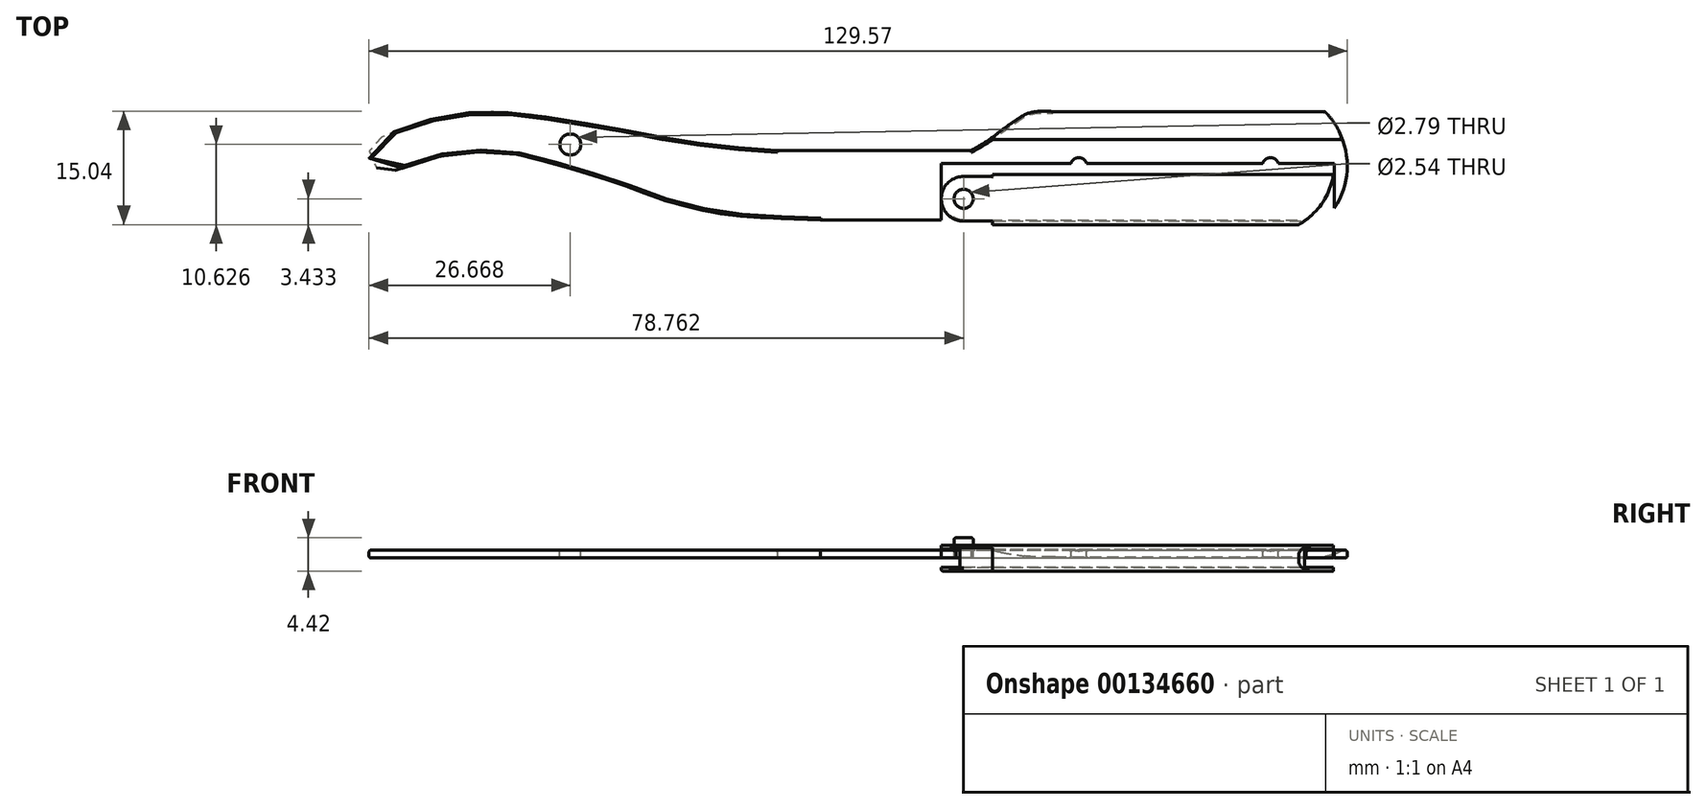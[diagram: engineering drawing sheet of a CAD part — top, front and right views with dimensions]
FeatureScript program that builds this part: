
annotation { "Feature Type Name" : "Feature", "Feature Type Description" : "" }
export const myFeature = defineFeature(function(context is Context, id is Id, definition is map)
    precondition{}
    {
        {
            var Q0;
            Q0=qCreatedBy(makeId("Top.planeOp"),FACE);
            var sketch = newSketch(context, id + "F0", { "sketchPlane" : qUnion([Q0])});
            skPoint(sketch, "E0", {"position": v(130.8, 0) * mm});
            skPoint(sketch, "E1", {"position": v(-103.94, -143.52) * mm});
            skPoint(sketch, "E2", {"position": v(0.55, 0.24) * mm});
            skPoint(sketch, "E3", {"position": v(0.4, 1.22) * mm});
            skPoint(sketch, "E4", {"position": v(0.7, 2.2) * mm});
            skPoint(sketch, "E5", {"position": v(1.36, 2.96) * mm});
            skPoint(sketch, "E6", {"position": v(5, 4.63) * mm});
            skPoint(sketch, "E7", {"position": v(9.58, 5.96) * mm});
            skPoint(sketch, "E8", {"position": v(14.71, 6.72) * mm});
            skPoint(sketch, "E9", {"position": v(19.41, 6.61) * mm});
            skPoint(sketch, "E10", {"position": v(22.67, 6.26) * mm});
            skPoint(sketch, "E11", {"position": v(23.56, 6.1) * mm});
            skPoint(sketch, "E12", {"position": v(33.06, 4.54) * mm});
            skPoint(sketch, "E13", {"position": v(37.97, 3.6) * mm});
            skPoint(sketch, "E14", {"position": v(42.95, 2.72) * mm});
            skPoint(sketch, "E15", {"position": v(46.9, 2.26) * mm});
            skPoint(sketch, "E16", {"position": v(51.6, 1.8) * mm});
            skPoint(sketch, "E17", {"position": v(54.47, 1.63) * mm});
            skPoint(sketch, "E18", {"position": v(80.16, 1.63) * mm});
            skPoint(sketch, "E19", {"position": v(82.68, 3.16) * mm});
            skPoint(sketch, "E20", {"position": v(83.83, 4.04) * mm});
            skPoint(sketch, "E21", {"position": v(85.06, 4.93) * mm});
            skPoint(sketch, "E22", {"position": v(86.43, 5.87) * mm});
            skPoint(sketch, "E23", {"position": v(87.8, 6.58) * mm});
            skPoint(sketch, "E24", {"position": v(89.43, 6.85) * mm});
            skPoint(sketch, "E25", {"position": v(91.29, 6.78) * mm});
            skPoint(sketch, "E26", {"position": v(127.01, 6.78) * mm});
            skPoint(sketch, "E27", {"position": v(128.33, 5.87) * mm});
            skPoint(sketch, "E28", {"position": v(129.3, 4.49) * mm});
            skPoint(sketch, "E29", {"position": v(130.18, 1.72) * mm});
            skPoint(sketch, "E30", {"position": v(130.35, -0.84) * mm});
            skPoint(sketch, "E31", {"position": v(129.95, -2.76) * mm});
            skPoint(sketch, "E32", {"position": v(128.97, -5.52) * mm});
            skPoint(sketch, "E33", {"position": v(127.42, -7.1) * mm});
            skPoint(sketch, "E34", {"position": v(127.01, -7.57) * mm});
            skPoint(sketch, "E35", {"position": v(60.22, -7.57) * mm});
            skPoint(sketch, "E36", {"position": v(53.63, -7.32) * mm});
            skPoint(sketch, "E37", {"position": v(47.48, -6.84) * mm});
            skPoint(sketch, "E38", {"position": v(41.94, -5.64) * mm});
            skPoint(sketch, "E39", {"position": v(38.32, -4.6) * mm});
            skPoint(sketch, "E40", {"position": v(34.93, -3.26) * mm});
            skPoint(sketch, "E41", {"position": v(22.9, 0.41) * mm});
            skPoint(sketch, "E42", {"position": v(19.37, 1.23) * mm});
            skPoint(sketch, "E43", {"position": v(15.74, 1.42) * mm});
            skPoint(sketch, "E44", {"position": v(11.4, 1.13) * mm});
            skPoint(sketch, "E45", {"position": v(8.54, 0.52) * mm});
            skPoint(sketch, "E46", {"position": v(5.77, 0) * mm});
            skPoint(sketch, "E47", {"position": v(4.05, -0.96) * mm});
            skPoint(sketch, "E48", {"position": v(2.62, -1.15) * mm});
            skPoint(sketch, "E49", {"position": v(1.82, -0.96) * mm});
            skPoint(sketch, "E50", {"position": v(1.25, -0.57) * mm});
            skPoint(sketch, "E51", {"position": v(0.81, -0.18) * mm});
            skLineSegment(sketch, "E52", {"start": v(91.29, 6.78) * mm, "end": v(127.01, 6.78) * mm});
            skLineSegment(sketch, "E53", {"start": v(60.22, -7.57) * mm, "end": v(127.01, -7.57) * mm});
            skLineSegment(sketch, "E54", {"start": v(54.47, 1.63) * mm, "end": v(80.16, 1.63) * mm});
            skFitSpline(sketch, "E55", {"points": [v(80.16, 1.63) * mm, v(82.68, 3.16) * mm, v(83.83, 4.04) * mm, v(85.06, 4.93) * mm, v(86.43, 5.87) * mm, v(87.8, 6.58) * mm, v(89.43, 6.85) * mm, v(91.29, 6.78) * mm], "startDerivative": vector(15.23, 8.8) * mm, "endDerivative": vector(12.83, -0.9) * mm});
            skArc(sketch, "E56", {"start": v(127.01, -7.57) * mm, "mid": v(129.97, -0.4) * mm, "end": v(127.01, 6.78) * mm});
            skFitSpline(sketch, "E57", {"points": [v(60.22, -7.57) * mm, v(53.63, -7.32) * mm, v(47.48, -6.84) * mm, v(41.94, -5.64) * mm, v(38.32, -4.6) * mm, v(34.93, -3.26) * mm, v(22.9, 0.41) * mm, v(19.37, 1.23) * mm, v(15.74, 1.42) * mm, v(11.4, 1.13) * mm, v(8.54, 0.52) * mm, v(4.05, -0.96) * mm, v(2.62, -1.15) * mm, v(1.82, -0.96) * mm, v(1.25, -0.57) * mm, v(0.81, -0.18) * mm, v(0.55, 0.24) * mm, v(0.4, 1.22) * mm, v(0.7, 2.2) * mm, v(1.36, 2.96) * mm, v(5, 4.63) * mm, v(9.58, 5.96) * mm, v(14.71, 6.72) * mm, v(19.41, 6.61) * mm, v(22.67, 6.26) * mm, v(23.56, 6.1) * mm, v(33.06, 4.54) * mm, v(37.97, 3.6) * mm, v(42.95, 2.72) * mm, v(46.9, 2.26) * mm, v(51.6, 1.8) * mm, v(54.47, 1.63) * mm], "startDerivative": vector(-147, 5.5) * mm, "endDerivative": vector(89.1, -4.43) * mm});
            skSolve(sketch);
        }
        {
            var Q0;
            Q0=qSketchRegion(id+"F0",true);
            extrude(context, id + "F1", {"entities" : qUnion([Q0]), "depth" : 1.02 * mm});
        }
        {
            var Q0;
            Q0=makeQuery(id+"F1.opExtrude","CAP_FACE",FACE,{"disambiguationData":[OSD([sQuery(id+"F0.wireOp",EDGE,"E52"),sQuery(id+"F0.wireOp",EDGE,"E53"),sQuery(id+"F0.wireOp",EDGE,"E54"),sQuery(id+"F0.wireOp",EDGE,"E55"),sQuery(id+"F0.wireOp",EDGE,"E56"),sQuery(id+"F0.wireOp",EDGE,"E57")])],"isStart":false});
            var sketch = newSketch(context, id + "F2", { "sketchPlane" : qUnion([Q0])});
            skCircle(sketch, "E58", {"center": v(119.81, -0.4) * mm, "radius": 1.08 * mm});
            skPoint(sketch, "E58.centerSnap0", {"position": v(129.97, -0.4) * mm});
            skCircle(sketch, "E59", {"center": v(94.41, -0.4) * mm, "radius": 1.08 * mm});
            skSolve(sketch);
        }
        {
            var Q0;
            Q0=makeQuery(id+"F2.imprint","IMPRINT",FACE,{"disambiguationData":[TD([[makeQuery(id+"F2.imprint","IMPRINT",EDGE,{"derivedFrom":sQuery(id+"F2.wireOp",EDGE,"E58")}),-1.0]])]});
            var sketch = newSketch(context, id + "F3", { "sketchPlane" : qUnion([Q0])});
            skCircle(sketch, "E60", {"center": v(27.07, 2.42) * mm, "radius": 1.4 * mm});
            skPoint(sketch, "E61", {"position": v(0.4, 1.03) * mm});
            skSolve(sketch);
        }
        {
            var Q0;
            Q0=qSketchRegion(id+"F3",true);
            extrude(context, id + "F4", {"entities" : qUnion([Q0]), "operationType" : NewBodyOperationType.REMOVE, "endBound" : BoundingType.THROUGH_ALL, "oppositeDirection" : true, "depth" : 25.4 * mm});
        }
        {
            var Q0;
            Q0=qSketchRegion(id+"F2",true);
            extrude(context, id + "F5", {"entities" : qUnion([Q0]), "operationType" : NewBodyOperationType.REMOVE, "endBound" : BoundingType.THROUGH_ALL, "oppositeDirection" : true, "depth" : 25.4 * mm});
        }
        {
            var Q0;
            Q0=qCreatedBy(makeId("Right.planeOp"),FACE);
            cPlane(context, id + "F6", {"entities" : qUnion([Q0]), "cplaneType" : CPlaneType.OFFSET, "offset" : 152.4 * mm, "width" : 152.4 * mm, "height" : 152.4 * mm});
        }
        {
            var Q0;
            Q0=qCreatedBy(id+"F6.planeOp",FACE);
            var sketch = newSketch(context, id + "F7", { "sketchPlane" : qUnion([Q0])});
            skLineSegment(sketch, "E62", {"start": v(6.86, 1.02) * mm, "end": v(6.86, 0.14) * mm});
            skLineSegment(sketch, "E63", {"start": v(6.86, 0.14) * mm, "end": v(3.05, 1.02) * mm});
            skLineSegment(sketch, "E64", {"start": v(3.05, 1.02) * mm, "end": v(6.86, 1.02) * mm});
            skSolve(sketch);
        }
        {
            var Q0;
            Q0=qSketchRegion(id+"F7",true);
            extrude(context, id + "F8", {"entities" : qUnion([Q0]), "operationType" : NewBodyOperationType.REMOVE, "oppositeDirection" : true, "depth" : 73.66 * mm});
        }
        {
            var Q0;
            Q0=makeQuery(id+"F1.opExtrude","CAP_FACE",FACE,{"disambiguationData":[OSD([sQuery(id+"F0.wireOp",EDGE,"E52"),sQuery(id+"F0.wireOp",EDGE,"E53"),sQuery(id+"F0.wireOp",EDGE,"E54"),sQuery(id+"F0.wireOp",EDGE,"E55"),sQuery(id+"F0.wireOp",EDGE,"E56"),sQuery(id+"F0.wireOp",EDGE,"E57")])],"isStart":false});
            var sketch = newSketch(context, id + "F9", { "sketchPlane" : qUnion([Q0])});
            skCircle(sketch, "E65", {"center": v(79.16, -4.78) * mm, "radius": 1.27 * mm});
            skPoint(sketch, "E66", {"position": v(129.96, 0) * mm});
            skSolve(sketch);
        }
        {
            var Q0;
            Q0=qSketchRegion(id+"F9",true);
            extrude(context, id + "F10", {"entities" : qUnion([Q0]), "operationType" : NewBodyOperationType.REMOVE, "endBound" : BoundingType.THROUGH_ALL, "oppositeDirection" : true, "depth" : 25.4 * mm});
        }
        {
            var Q0;
            Q0=makeQuery(id+"F1.opExtrude","CAP_EDGE",EDGE,{"disambiguationData":[OSD([sQuery(id+"F0.wireOp",EDGE,"E57")])],"isStart":false});
            var Q1;
            Q1=makeQuery(id+"F1.opExtrude","CAP_EDGE",EDGE,{"disambiguationData":[OSD([sQuery(id+"F0.wireOp",EDGE,"E53")])],"isStart":false});
            var Q2;
            Q2=makeQuery(id+"F1.opExtrude","CAP_EDGE",EDGE,{"disambiguationData":[OSD([sQuery(id+"F0.wireOp",EDGE,"E56")])],"isStart":false});
            var Q3;
            Q3=makeQuery(id+"F1.opExtrude","CAP_EDGE",EDGE,{"disambiguationData":[OSD([sQuery(id+"F0.wireOp",EDGE,"E54")])],"isStart":false});
            var Q4;
            Q4=makeQuery(id+"F1.opExtrude","CAP_EDGE",EDGE,{"disambiguationData":[OSD([sQuery(id+"F0.wireOp",EDGE,"E55")])],"isStart":false});
            var Q5;
            Q5=makeQuery(id+"F1.opExtrude","CAP_EDGE",EDGE,{"disambiguationData":[OSD([sQuery(id+"F0.wireOp",EDGE,"E53")])],"isStart":true});
            var Q6;
            Q6=makeQuery(id+"F1.opExtrude","CAP_EDGE",EDGE,{"disambiguationData":[OSD([sQuery(id+"F0.wireOp",EDGE,"E57")])],"isStart":true});
            var Q7;
            Q7=makeQuery(id+"F1.opExtrude","CAP_EDGE",EDGE,{"disambiguationData":[OSD([sQuery(id+"F0.wireOp",EDGE,"E54")])],"isStart":true});
            var Q8;
            Q8=makeQuery(id+"F1.opExtrude","CAP_EDGE",EDGE,{"disambiguationData":[OSD([sQuery(id+"F0.wireOp",EDGE,"E55")])],"isStart":true});
            var Q9;
            Q9=makeQuery(id+"F1.opExtrude","CAP_EDGE",EDGE,{"disambiguationData":[OSD([sQuery(id+"F0.wireOp",EDGE,"E52")])],"isStart":true});
            var Q10;
            Q10=makeQuery(id+"F1.opExtrude","CAP_EDGE",EDGE,{"disambiguationData":[OSD([sQuery(id+"F0.wireOp",EDGE,"E56")])],"isStart":true});
            var Q11;
            Q11=makeQuery(id+"F5.boolean.opBoolean","COPY",FACE,{"derivedFrom":makeQuery(id+"F5.opExtrude","SWEPT_FACE",FACE,{"disambiguationData":[OSD([sQuery(id+"F2.wireOp",EDGE,"E59")])]})});
            var Q12;
            Q12=makeQuery(id+"F5.boolean.opBoolean","COPY",FACE,{"derivedFrom":makeQuery(id+"F5.opExtrude","SWEPT_FACE",FACE,{"disambiguationData":[OSD([sQuery(id+"F2.wireOp",EDGE,"E58")])]})});
            fillet(context, id + "F11", {"entities" : qUnion([Q0, Q1, Q2, Q3, Q4, Q5, Q6, Q7, Q8, Q9, Q10, Q11, Q12]), "radius" : 0.25 * mm, "tangentPropagation" : true, "allowEdgeOverflow" : false});
        }
        {
            var Q0;
            Q0=qCreatedBy(id+"F6.planeOp",FACE);
            cPlane(context, id + "F12", {"entities" : qUnion([Q0]), "cplaneType" : CPlaneType.OFFSET, "offset" : 24.13 * mm, "oppositeDirection" : true, "width" : 152.4 * mm, "height" : 152.4 * mm});
        }
        {
            var Q0;
            Q0=qCreatedBy(id+"F12.planeOp",FACE);
            var sketch = newSketch(context, id + "F13", { "sketchPlane" : qUnion([Q0])});
            skLineSegment(sketch, "E67", {"start": v(-0.08, 1.14) * mm, "end": v(-7.7, 1.14) * mm});
            skLineSegment(sketch, "E68", {"start": v(-7.7, 1.14) * mm, "end": v(-7.7, -1.24) * mm});
            skLineSegment(sketch, "E69", {"start": v(-7.7, -1.24) * mm, "end": v(-0.08, -1.24) * mm});
            skLineSegment(sketch, "E70.0", {"start": v(-8.2, -1.75) * mm, "end": v(-0.08, -1.75) * mm});
            skLineSegment(sketch, "E70.1", {"start": v(-8.2, 1.65) * mm, "end": v(-8.2, -1.75) * mm});
            skLineSegment(sketch, "E70.2", {"start": v(-0.08, 1.65) * mm, "end": v(-8.2, 1.65) * mm});
            skLineSegment(sketch, "E71", {"start": v(-0.08, 1.65) * mm, "end": v(-0.08, 1.14) * mm});
            skLineSegment(sketch, "E72", {"start": v(-0.08, -1.24) * mm, "end": v(-0.08, -1.75) * mm});
            skSolve(sketch);
        }
        {
            var Q0;
            Q0 = qSketchRegion(id + "F13", true);
            extrude(context, id + "F14", {"entities" : qUnion([Q0]), "oppositeDirection" : true, "depth" : 52.07 * mm});
        }
        {
            var Q0;
            Q0=makeQuery(id+"F14.opExtrude","SWEPT_FACE",FACE,{"disambiguationData":[OSD([sQuery(id+"F13.wireOp",EDGE,"E70.2")])]});
            var sketch = newSketch(context, id + "F15", { "sketchPlane" : qUnion([Q0])});
            skLineSegment(sketch, "E73", {"start": v(128.27, -0.08) * mm, "end": v(128.27, 1.35) * mm, "construction": true});
            skArc(sketch, "E74", {"start": v(128.27, -0.08) * mm, "mid": v(127, -4.78) * mm, "end": v(123.54, -8.2) * mm});
            skLineSegment(sketch, "E75", {"start": v(123.54, -8.2) * mm, "end": v(128.27, -8.2) * mm});
            skLineSegment(sketch, "E76", {"start": v(128.27, -8.2) * mm, "end": v(128.27, -0.08) * mm});
            skSolve(sketch);
        }
        {
            var Q0;
            Q0 = qSketchRegion(id + "F15", true);
            extrude(context, id + "F16", {"entities" : qUnion([Q0]), "operationType" : NewBodyOperationType.REMOVE, "endBound" : BoundingType.THROUGH_ALL, "oppositeDirection" : true, "depth" : 25.4 * mm});
        }
        {
            var Q0;
            Q0=makeQuery(id+"F14.opExtrude","SWEPT_FACE",FACE,{"disambiguationData":[OSD([sQuery(id+"F13.wireOp",EDGE,"E70.2")])]});
            var sketch = newSketch(context, id + "F17", { "sketchPlane" : qUnion([Q0])});
            skArc(sketch, "E77", {"start": v(79.16, -1.81) * mm, "mid": v(76.2, -4.78) * mm, "end": v(79.16, -7.74) * mm});
            skLineSegment(sketch, "E78", {"start": v(79.16, -7.74) * mm, "end": v(83, -7.74) * mm});
            skLineSegment(sketch, "E79", {"start": v(83, -7.74) * mm, "end": v(83, -8.2) * mm});
            skLineSegment(sketch, "E80", {"start": v(83, -8.2) * mm, "end": v(76.2, -8.2) * mm});
            skLineSegment(sketch, "E81", {"start": v(76.2, -8.2) * mm, "end": v(76.2, -4.78) * mm});
            skLineSegment(sketch, "E82", {"start": v(79.16, -1.81) * mm, "end": v(83, -1.81) * mm});
            skLineSegment(sketch, "E83", {"start": v(83, -1.81) * mm, "end": v(83, -1.54) * mm});
            skLineSegment(sketch, "E84", {"start": v(83, -1.54) * mm, "end": v(128.15, -1.54) * mm});
            skLineSegment(sketch, "E85.0", {"start": v(76.2, -0.08) * mm, "end": v(128.27, -0.08) * mm});
            skLineSegment(sketch, "E86.0", {"start": v(76.2, -8.2) * mm, "end": v(83, -8.2) * mm});
            skArc(sketch, "E86.1", {"start": v(128.27, -0.08) * mm, "mid": v(128.24, -0.81) * mm, "end": v(128.15, -1.54) * mm});
            skPoint(sketch, "E87.orphan", {"position": v(123.54, -8.2) * mm});
            skLineSegment(sketch, "E88", {"start": v(76.2, -0.08) * mm, "end": v(76.2, -4.78) * mm});
            skSolve(sketch);
        }
        {
            var Q0;
            Q0 = qSketchRegion(id + "F17", true);
            extrude(context, id + "F18", {"entities" : qUnion([Q0]), "operationType" : NewBodyOperationType.REMOVE, "endBound" : BoundingType.THROUGH_ALL, "oppositeDirection" : true, "depth" : 25.4 * mm});
        }
        {
            var Q0;
            Q0=makeQuery(id+"F14.opExtrude","SWEPT_FACE",FACE,{"disambiguationData":[OSD([sQuery(id+"F13.wireOp",EDGE,"E70.2")])]});
            var sketch = newSketch(context, id + "F19", { "sketchPlane" : qUnion([Q0])});
            skCircle(sketch, "E89", {"center": v(79.16, -4.78) * mm, "radius": 1.27 * mm});
            skSolve(sketch);
        }
        {
            var Q0;
            Q0 = qSketchRegion(id + "F19", true);
            extrude(context, id + "F20", {"entities" : qUnion([Q0]), "operationType" : NewBodyOperationType.ADD, "depth" : 1.02 * mm});
        }
        {
            var Q0;
            Q0=makeQuery(id+"F14.opExtrude","SWEPT_EDGE",EDGE,{"disambiguationData":[OSD([sQuery(id+"F13.wireOp",EDGE,"E70.1"),sQuery(id+"F13.wireOp",EDGE,"E70.2")])]});
            var Q1;
            Q1=makeQuery(id+"F14.opExtrude","SWEPT_EDGE",EDGE,{"disambiguationData":[OSD([sQuery(id+"F13.wireOp",EDGE,"E70.0"),sQuery(id+"F13.wireOp",EDGE,"E70.1")])]});
            fillet(context, id + "F21", {"entities" : qUnion([Q0, Q1]), "radius" : 1.27 * mm, "tangentPropagation" : true, "allowEdgeOverflow" : false});
        }
        {
            var Q0;
            Q0=makeQuery(id+"F18.boolean.opBoolean","COPY",EDGE,{"derivedFrom":makeQuery(id+"F18.opExtrude","CAP_EDGE",EDGE,{"disambiguationData":[OSD([sQuery(id+"F17.wireOp",EDGE,"E84")])],"isStart":true})});
            var Q1;
            {var subQ0=sQuery(id+"F17.wireOp",EDGE,"E77");Q1=makeQuery(id+"F18.boolean.opBoolean","TWEAK_EDGE",EDGE,{"derivedFrom":[makeQuery(id+"F18.opExtrude","CAP_EDGE",EDGE,{"disambiguationData":[OSD([subQ0]),TDD([makeQuery(id+"F17.imprint","IMPRINT",EDGE,{"disambiguationData":[TD([[makeQuery(id+"F17.imprint","INTERSECT",VERTEX,{"derivedFrom":[subQ0,sQuery(id+"F17.wireOp",EDGE,"E82")]}),-1.0]])],"derivedFrom":subQ0})])],"isStart":true}),makeQuery(id+"F18.opExtrude","CAP_EDGE",EDGE,{"disambiguationData":[OSD([subQ0]),TDD([makeQuery(id+"F17.imprint","IMPRINT",EDGE,{"disambiguationData":[TD([[makeQuery(id+"F17.imprint","INTERSECT",VERTEX,{"derivedFrom":[subQ0,sQuery(id+"F17.wireOp",EDGE,"E78")]}),1.0]])],"derivedFrom":subQ0})])],"isStart":true})]});}
            var Q2;
            Q2=makeQuery(id+"F20.opExtrude","CAP_FACE",FACE,{"disambiguationData":[OSD([sQuery(id+"F19.wireOp",EDGE,"E89")])],"isStart":false});
            var Q3;
            Q3=makeQuery(id+"F16.boolean.opBoolean","COPY",EDGE,{"derivedFrom":makeQuery(id+"F16.opExtrude","CAP_EDGE",EDGE,{"disambiguationData":[OSD([sQuery(id+"F15.wireOp",EDGE,"E74")])],"isStart":true})});
            var Q4;
            Q4=makeQuery(id+"F18.boolean.opBoolean","INTERSECT",EDGE,{"derivedFrom":[makeQuery(id+"F14.opExtrude","SWEPT_FACE",FACE,{"disambiguationData":[OSD([sQuery(id+"F13.wireOp",EDGE,"E70.0")])]}),makeQuery(id+"F18.opExtrude","SWEPT_FACE",FACE,{"disambiguationData":[OSD([sQuery(id+"F17.wireOp",EDGE,"E84")])]})]});
            var Q5;
            {var subQ0=sQuery(id+"F17.wireOp",EDGE,"E77");Q5=makeQuery(id+"F18.boolean.opBoolean","INTERSECT",EDGE,{"derivedFrom":[makeQuery(id+"F14.opExtrude","SWEPT_FACE",FACE,{"disambiguationData":[OSD([sQuery(id+"F13.wireOp",EDGE,"E70.0")])]}),makeQuery(id+"F18.opExtrude","SWEPT_FACE",FACE,{"disambiguationData":[OSD([subQ0]),TDD([makeQuery(id+"F17.imprint","IMPRINT",EDGE,{"disambiguationData":[TD([[makeQuery(id+"F17.imprint","INTERSECT",VERTEX,{"derivedFrom":[subQ0,sQuery(id+"F17.wireOp",EDGE,"E82")]}),-1.0]])],"derivedFrom":subQ0})])]}),makeQuery(id+"F18.opExtrude","SWEPT_FACE",FACE,{"disambiguationData":[OSD([subQ0]),TDD([makeQuery(id+"F17.imprint","IMPRINT",EDGE,{"disambiguationData":[TD([[makeQuery(id+"F17.imprint","INTERSECT",VERTEX,{"derivedFrom":[subQ0,sQuery(id+"F17.wireOp",EDGE,"E78")]}),1.0]])],"derivedFrom":subQ0})])]})]});}
            fillet(context, id + "F22", {"entities" : qUnion([Q0, Q1, Q2, Q3, Q4, Q5]), "radius" : 0.25 * mm, "tangentPropagation" : true, "allowEdgeOverflow" : false});
        }
    });
